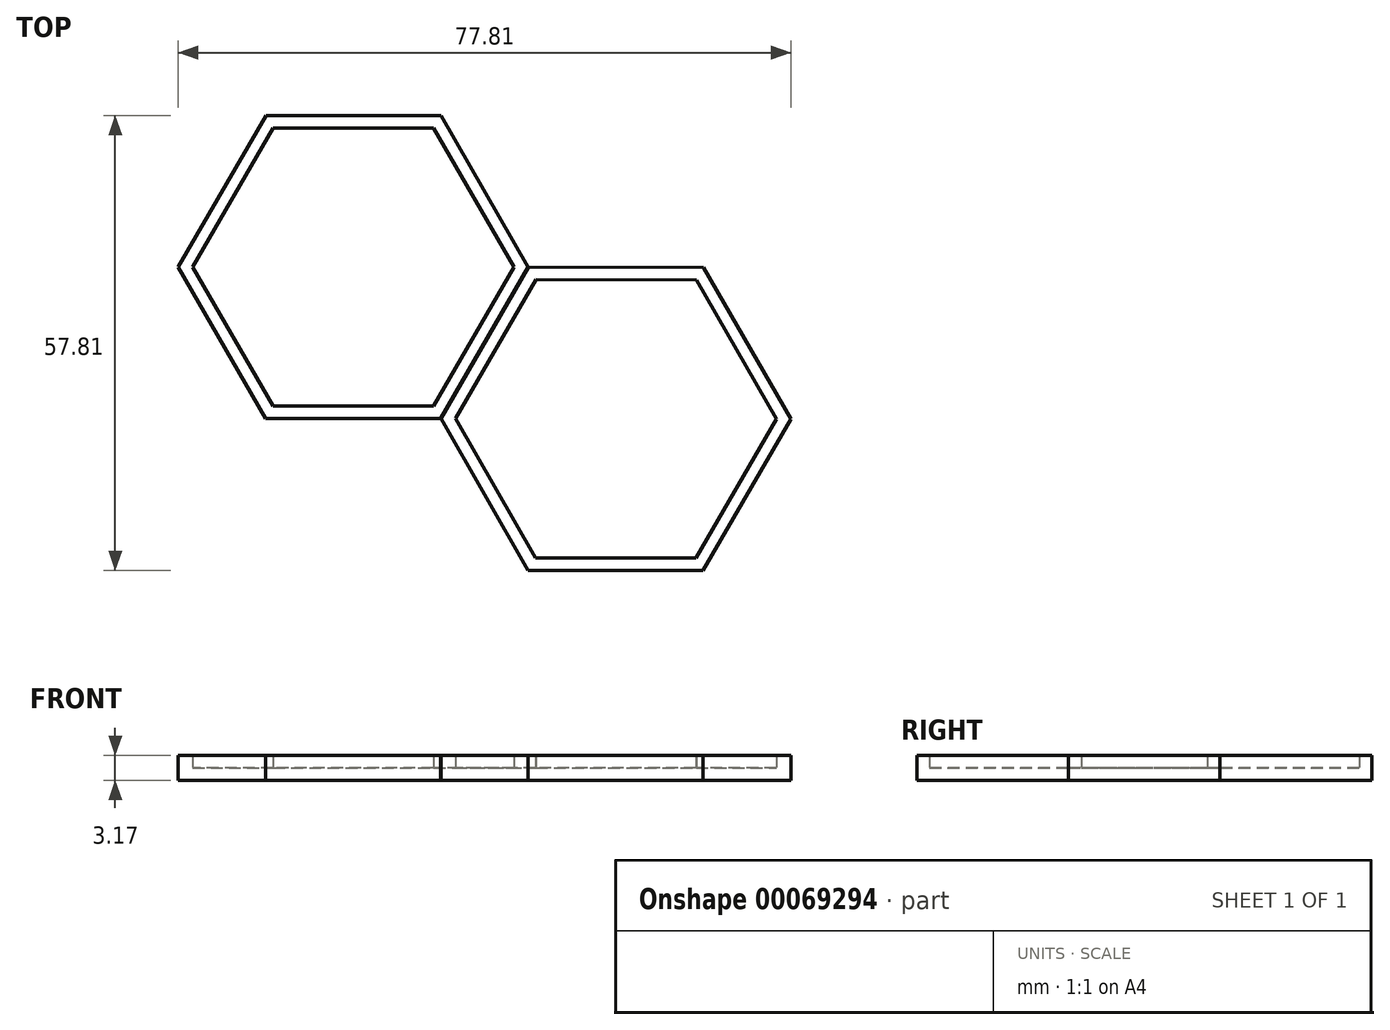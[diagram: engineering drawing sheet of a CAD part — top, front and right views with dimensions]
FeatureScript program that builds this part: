
annotation { "Feature Type Name" : "Feature", "Feature Type Description" : "" }
export const myFeature = defineFeature(function(context is Context, id is Id, definition is map)
    precondition{}
    {
        {
            var Q0;
            Q0=qCreatedBy(makeId("Top.planeOp"),FACE);
            var sketch = newSketch(context, id + "F0", { "sketchPlane" : qUnion([Q0])});
            skCircle(sketch, "E0.cCircle", {"center": v(0, 0) * mm, "radius": 19.25 * mm, "construction": true});
            skLineSegment(sketch, "E0.0", {"start": v(11.14, 19.23) * mm, "end": v(22.22, -0.03) * mm});
            skLineSegment(sketch, "E0.1", {"start": v(22.22, -0.03) * mm, "end": v(11.09, -19.26) * mm});
            skLineSegment(sketch, "E0.2", {"start": v(11.09, -19.26) * mm, "end": v(-11.14, -19.23) * mm});
            skLineSegment(sketch, "E0.3", {"start": v(-11.14, -19.23) * mm, "end": v(-22.22, 0.03) * mm});
            skLineSegment(sketch, "E0.4", {"start": v(-22.23, 0.03) * mm, "end": v(-11.09, 19.26) * mm});
            skLineSegment(sketch, "E0.5", {"start": v(-11.09, 19.26) * mm, "end": v(11.14, 19.23) * mm});
            skPoint(sketch, "E0.0.midPoint", {"position": v(16.68, 9.6) * mm});
            skSolve(sketch);
        }
        {
            var Q0;
            Q0=qSketchRegion(id+"F0",true);
            extrude(context, id + "F1", {"entities" : qUnion([Q0]), "depth" : 3.17 * mm});
        }
        {
            var Q0;
            Q0=makeQuery(id+"F1.opExtrude","CAP_FACE",FACE,{"disambiguationData":[OSD([sQuery(id+"F0.wireOp",EDGE,"E0.0"),sQuery(id+"F0.wireOp",EDGE,"E0.1"),sQuery(id+"F0.wireOp",EDGE,"E0.2"),sQuery(id+"F0.wireOp",EDGE,"E0.3"),sQuery(id+"F0.wireOp",EDGE,"E0.4"),sQuery(id+"F0.wireOp",EDGE,"E0.5")])],"isStart":false});
            shell(context, id + "F2", {"entities" : qUnion([Q0]), "thickness" : 1.59 * mm});
        }
        {
            var Q0;
            Q0=makeQuery(id+"F1.opExtrude","SWEPT_BODY",BODY,{"disambiguationData":[OSD([sQuery(id+"F0.wireOp",EDGE,"E0.0"),sQuery(id+"F0.wireOp",EDGE,"E0.1"),sQuery(id+"F0.wireOp",EDGE,"E0.2"),sQuery(id+"F0.wireOp",EDGE,"E0.3"),sQuery(id+"F0.wireOp",EDGE,"E0.4"),sQuery(id+"F0.wireOp",EDGE,"E0.5")])]});
            transform(context, id + "F3", {"entities" : qUnion([Q0]), "transformType" : TransformType.TRANSLATION_3D, "dx" : 33.36 * mm, "dy" : -19.29 * mm, "dz" : 0 * mm, "makeCopy" : true});
        }
    });
